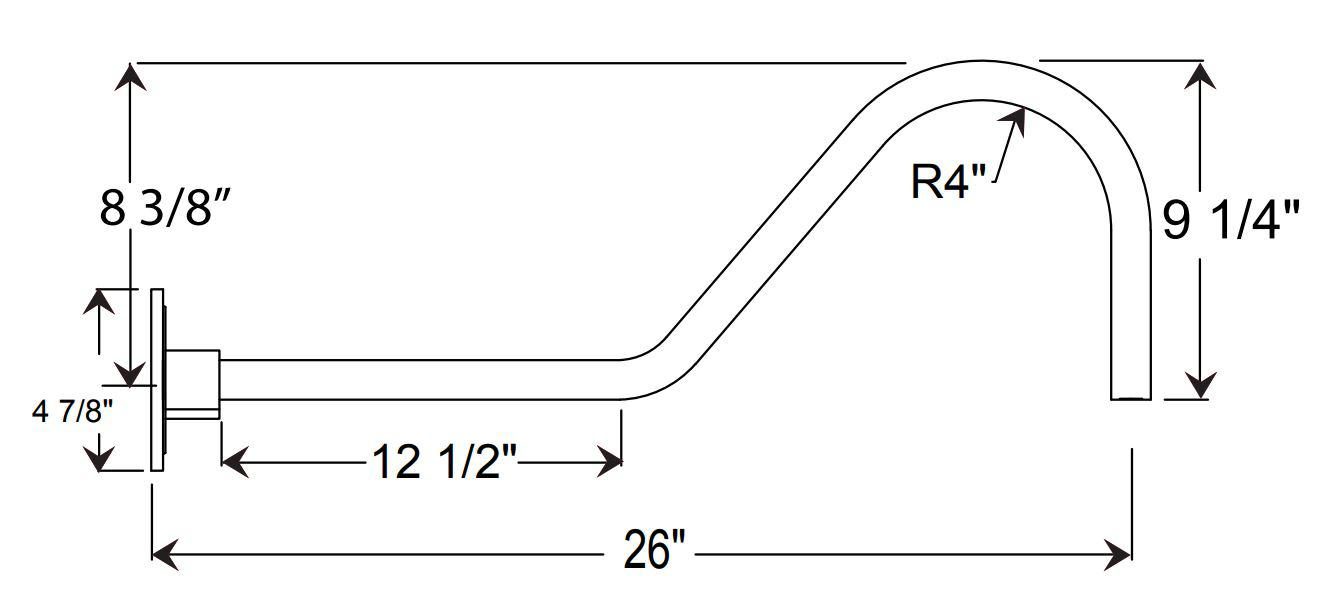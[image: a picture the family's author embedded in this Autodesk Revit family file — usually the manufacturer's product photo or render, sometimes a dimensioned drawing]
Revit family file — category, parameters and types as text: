
# Revit family: Orchid 16,20,24,30 LED
name_source: partatom
category: Lighting Fixtures
units: mm (PartAtom-declared; Revit-internal decimal feet)

## family parameters
Always vertical = Yes
Cut with Voids When Loaded = No
Light Source = Yes
OmniClass Number = 23.80.70.00
OmniClass Title = Lighting
Part Type = Normal
Room Calculation Point = No
Round Connector Dimension = Use Diameter
Shared = No
Work Plane-Based = No

## types (4) — shared parameters
Body Colour = Spun aluminium
Body Material = body
CRI = >90
Color Filter = 16777215
Construction Material = Heavy Duty spun aluminum.
Default Elevation = 0' - 0"
Description = 120-277 Voltage
Dimming = 1%
Dimming Lamp Color Temperature Shift = <None>
Efficiency = 65-125 lumens per watt
Fixture Finish = Fixture Finish
GLASS = Glass
Lamp = LED
Life = L70 50,000 hours
Load Classification = Lighting
Manufacturer = ANP Lighting
Power Factor = 1
Tilt Angle = 90.00°
URL = https://www.anplighting.com
Voltage = 277 V
Warranty = 5 year limited warranty

## per-type parameters (varying)
| type | Apparent Load | Fixture Diameter | Fixture Height | MDO16 | MDO20 | MDO24 | MDO30 | Photometric Web File | Wattage Comments | Weight |
| MDO16 | 10 VA | 1' - 4" | 0' - 6" | Yes | No | No | No | MDO16M010LD35K.IES | 10W | 7 lbs |
| MDO20 | 16 VA | 1' - 8" | 0' - 6 1/2" | No | Yes | No | No | MDO20M016LD35K.IES | 16W | 7.5 lbs |
| MDO24 | 24 VA | 2' - 0" | 0' - 8" | No | No | Yes | No | MDO24M024LD35K.IES | 24W | 8.0 lbs |
| MDO30 | 24 VA | 1' - 8" | 0' - 10" | No | No | No | Yes | MDO24M024LD35K.IES | 24W | 8.5 lbs |

note: column(s) folded — value = type name in every type: Model

## geometry (parser evidence)
native form markers: Sweep x31
no freeform markers — native parametric forms only
